# Revit family: Domotics-DomesticRanges-GEWISS-SYSTEM_POWER-SOCKET-OUTLET_AUS
name_source: partatom
category: Apparecchi elettrici
revit_build: Autodesk Revit 2016 (Build: 20161004_0715(x64)
units: mm (PartAtom-declared; Revit-internal decimal feet)

## family parameters
Condiviso = Sì
Host = Superficie
Mantenere orientamento annotazione = Sì
Punto di calcolo locali = Sì
Quota connettore circolare = Usa diametro
Taglio con vuoti quando caricato = Sì
Tipo di parte = Normale

## types (4) — shared parameters
Carico apparente = 0 VA
Catalogue = DOMOTICS
Catalogue Range = SYSTEM - DOMESTIC RANGE
Description. = Australia
Electrocod = 0131
For plug pins = Flat
IDF = 1145ae5c-4ab5-4dba-b292-451ff308354a
IDT = e052d7e5-2dfb-43db-bd48-dbccbcd1e75c
Immagine tipo = GW21357.jpg
N. poli = 1
No. SYSTEM modules = 2
Produttore = GEWISS S.p.A.
Prospetto di default = 1219 mm
SEO = Socket outlet
Standard = Australian
Standard: = Australian
TIPO_ = System Prese Australia_GENERICO : GW21357 Presa 2P+T 10A standard Australiano nero
TXT ELETTRICO = 10
Technical sheet = https://www.gewiss.com
URL = https://www.gewiss.com
Version file RFA = 19.4
Volt = 230 V
Voltage = 250 V ac
Voltage: = 250 V ac

## per-type parameters (varying)
| type | Colour | Description: | Descrizione | EAN code | Modello |
| GW21356 - 15A 2P+E austr.socket-outlet black | Black | 2P+E - 15A | 15A 2P+E AUSTR.SOCKET-OUTLET SY/BK | 8011564222267 | GW21356 |
| GW20357 - 10A 2P+E austr.socket-outlet white | White | 2P+E - 10A | 10A 2P+E AUSTR.SOCKET-OUTLET SY/WT | 8011564222236 | GW20357 |
| GW20356 - 15A 2P+E austr.socket-outlet white | White | 2P+E - 15A | 15A 2P+E AUSTR.SOCKET-OUTLET SY/WT | 8011564222250 | GW20356 |
| GW21357 - 10A 2P+E austr.socket-outlet black | Black | 2P+E - 10A | 10A 2P+E AUSTR.SOCKET-OUTLET SY/BK | 8011564222229 | GW21357 |

## geometry (parser evidence)
native form markers: Sweep x2
no freeform markers — native parametric forms only
